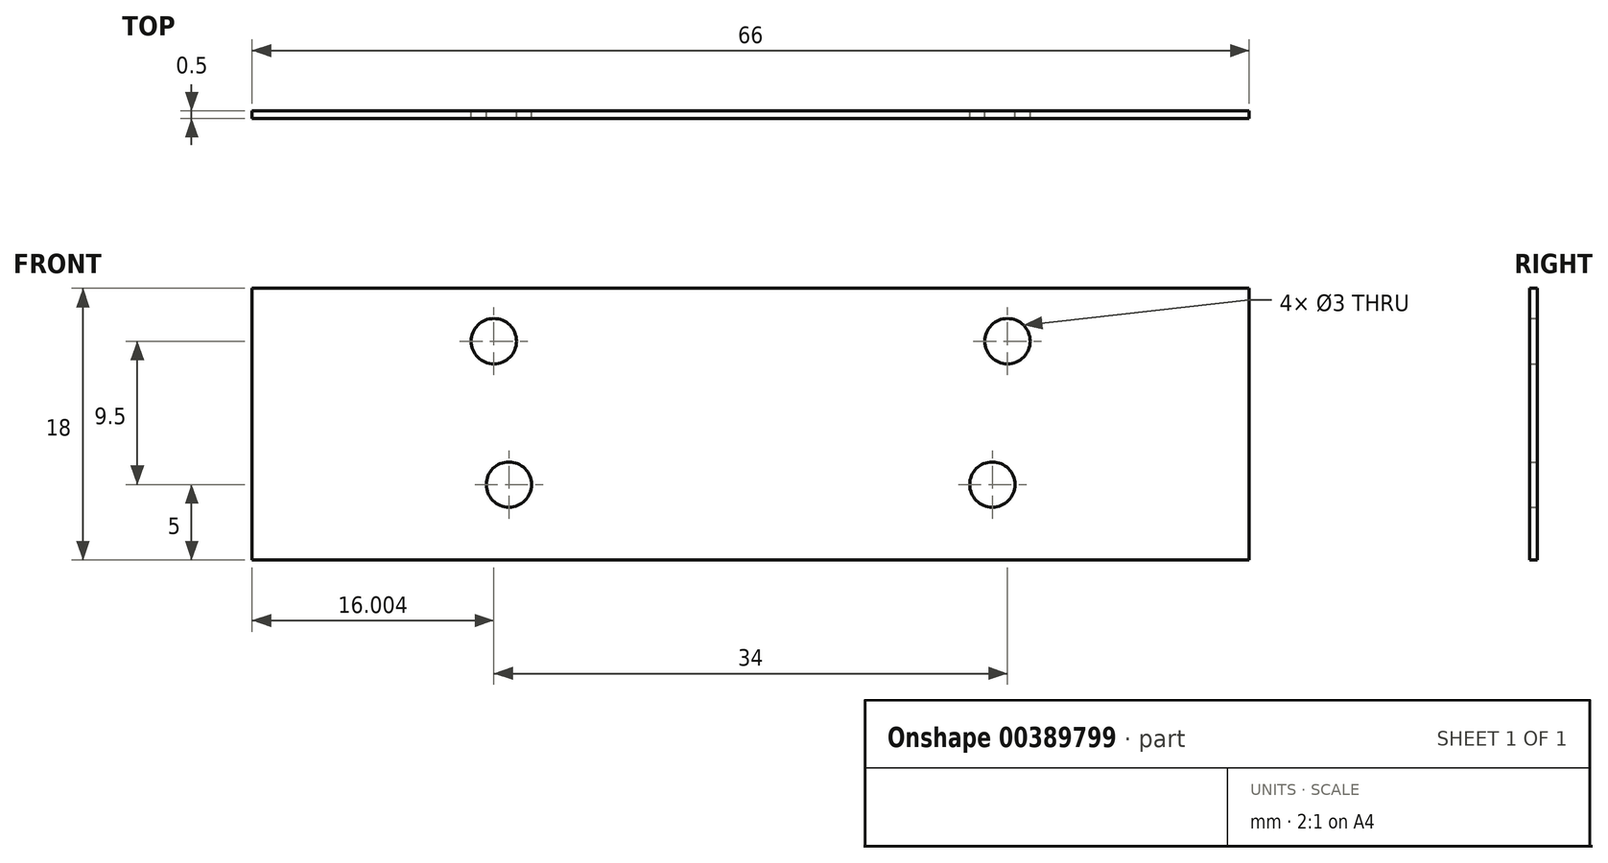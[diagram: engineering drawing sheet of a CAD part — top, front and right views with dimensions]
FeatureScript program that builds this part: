
annotation { "Feature Type Name" : "Feature", "Feature Type Description" : "" }
export const myFeature = defineFeature(function(context is Context, id is Id, definition is map)
    precondition{}
    {
        {
            var Q0;
            Q0=qCreatedBy(makeId("Front.planeOp"),FACE);
            var sketch = newSketch(context, id + "F0", { "sketchPlane" : qUnion([Q0])});
            skLineSegment(sketch, "E0.bottom", {"start": v(-23.88, 8) * mm, "end": v(42.12, 8) * mm});
            skLineSegment(sketch, "E0.top", {"start": v(-23.88, 0) * mm, "end": v(42.12, 0) * mm});
            skLineSegment(sketch, "E0.left", {"start": v(-23.88, 8) * mm, "end": v(-23.88, 0) * mm});
            skLineSegment(sketch, "E0.right", {"start": v(42.12, 8) * mm, "end": v(42.12, 0) * mm});
            skCircle(sketch, "E1", {"center": v(-7.88, 4.5) * mm, "radius": 1.5 * mm});
            skCircle(sketch, "E2", {"center": v(26.12, 4.5) * mm, "radius": 1.5 * mm});
            skLineSegment(sketch, "E3.top", {"start": v(-23.88, -10) * mm, "end": v(42.12, -10) * mm});
            skLineSegment(sketch, "E3.left", {"start": v(-23.88, 0) * mm, "end": v(-23.88, -10) * mm});
            skLineSegment(sketch, "E3.right", {"start": v(42.12, 0) * mm, "end": v(42.12, -10) * mm});
            skCircle(sketch, "E4", {"center": v(-6.88, -5) * mm, "radius": 1.5 * mm});
            skCircle(sketch, "E5", {"center": v(25.12, -5) * mm, "radius": 1.5 * mm});
            skSolve(sketch);
        }
        {
            var Q0;
            Q0 = qSketchRegion(id + "F0", true);
            extrude(context, id + "F1", {"entities" : qUnion([Q0]), "depth" : 0.5 * mm});
        }
    });
